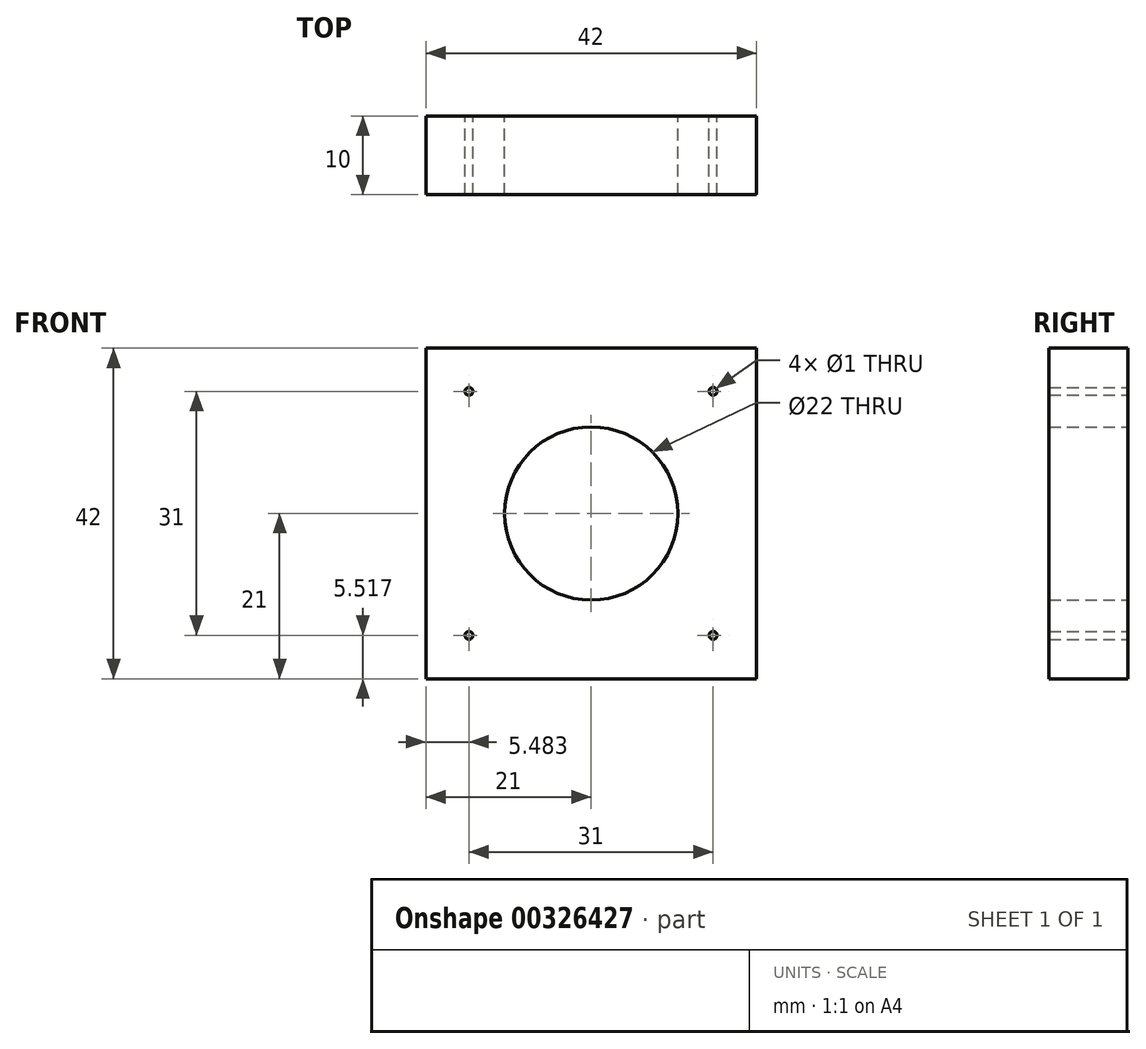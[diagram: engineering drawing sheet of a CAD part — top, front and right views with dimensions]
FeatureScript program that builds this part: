
annotation { "Feature Type Name" : "Feature", "Feature Type Description" : "" }
export const myFeature = defineFeature(function(context is Context, id is Id, definition is map)
    precondition{}
    {
        {
            var Q0;
            Q0=qCreatedBy(makeId("Front.planeOp"),FACE);
            var sketch = newSketch(context, id + "F0", { "sketchPlane" : qUnion([Q0])});
            skLineSegment(sketch, "E0.bottom", {"start": v(21, 21) * mm, "end": v(-21, 21) * mm});
            skLineSegment(sketch, "E0.top", {"start": v(21, -21) * mm, "end": v(-21, -21) * mm});
            skLineSegment(sketch, "E0.left", {"start": v(21, 21) * mm, "end": v(21, -21) * mm});
            skLineSegment(sketch, "E0.right", {"start": v(-21, 21) * mm, "end": v(-21, -21) * mm});
            skPoint(sketch, "E0.middle", {"position": v(0, 0) * mm});
            skCircle(sketch, "E1", {"center": v(0, 0) * mm, "radius": 11 * mm});
            skPoint(sketch, "E2.middle", {"position": v(-0.02, 0.02) * mm});
            skCircle(sketch, "E3", {"center": v(-15.52, 15.52) * mm, "radius": 0.5 * mm});
            skCircle(sketch, "E4", {"center": v(15.48, 15.52) * mm, "radius": 0.5 * mm});
            skCircle(sketch, "E5", {"center": v(-15.52, -15.48) * mm, "radius": 0.5 * mm});
            skCircle(sketch, "E6", {"center": v(15.48, -15.48) * mm, "radius": 0.5 * mm});
            skSolve(sketch);
        }
        {
            var Q0;
            Q0=makeQuery(id+"F0.imprint","IMPRINT",FACE,{"disambiguationData":[TD([[makeQuery(id+"F0.imprint","IMPRINT",EDGE,{"derivedFrom":sQuery(id+"F0.wireOp",EDGE,"E0.bottom")}),1.0]])]});
            extrude(context, id + "F1", {"entities" : qUnion([Q0]), "depth" : 10 * mm, "offsetDistance" : 25 * mm});
        }
    });
